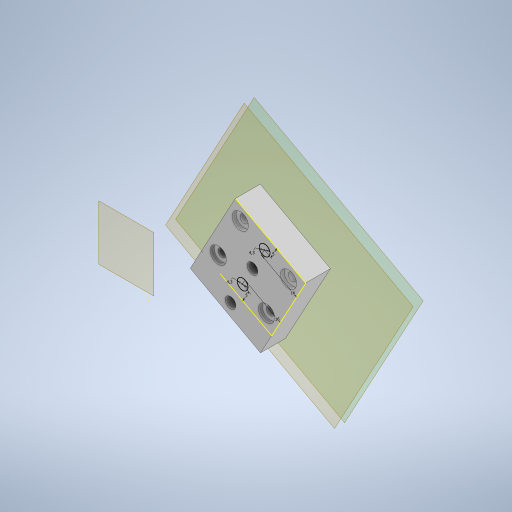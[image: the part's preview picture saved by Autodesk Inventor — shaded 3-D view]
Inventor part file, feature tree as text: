
AUTODESK INVENTOR PART (.ipt)
format: ipt  version: 2024.2 (Build 282272000, 272)  size: 314,880 bytes
history: native  units: mm
features: other x7, sketch x6, extrude x5, projected_geometry x1
ambient origin geometry x8: Origin, YZ Plane, XZ Plane, XY Plane, X Axis, Y Axis, Z Axis, Center Point
bodies: Body1 (feature_tree)
feature tree (19):
  other  "Твердое тело1"
  other  "РабПлоскость1"
  other  "РабПлоскость2"
  extrude  "Выдавливание1"  Depth=5.0mm
  sketch  "Эскиз3"
  other  "РабПлоскость3"
  extrude  "Выдавливание3"  Depth=5.0mm
  extrude  "Выдавливание4"  Depth=5.0mm
  sketch  "Эскиз6"
  extrude  "Выдавливание5"  Depth=5.0mm
  extrude  "Выдавливание6"  Depth=4.3mm
  sketch  "Эскиз2"
  sketch  "Эскиз4"
  sketch  "Эскиз5"
  projected_geometry  "Спроецированная петля1"
  sketch  "Эскиз7"
  other  "<userpath>\Documents\Artist\3D\каретка.iam"
  other  "каретка.iam"
  other  "ANY:5"
